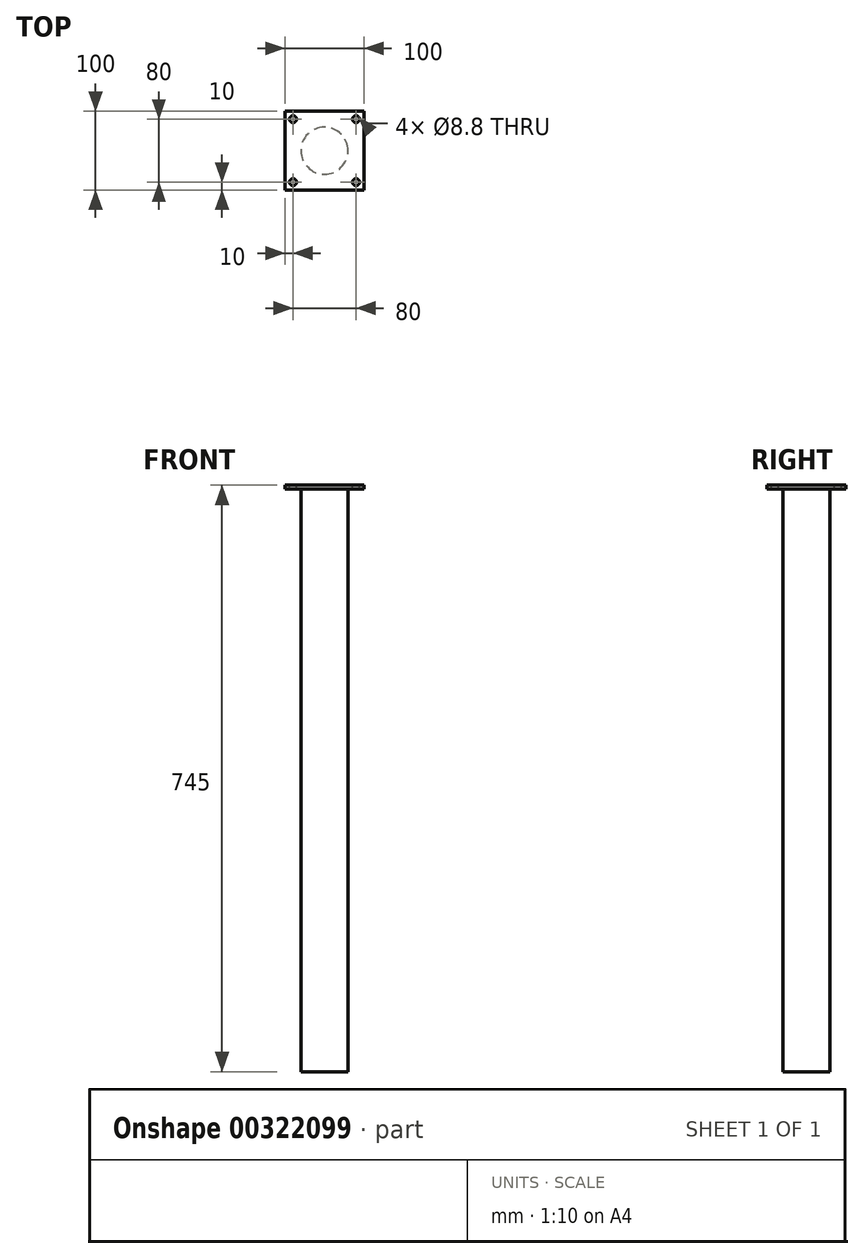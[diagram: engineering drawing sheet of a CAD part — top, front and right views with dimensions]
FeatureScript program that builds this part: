
annotation { "Feature Type Name" : "Feature", "Feature Type Description" : "" }
export const myFeature = defineFeature(function(context is Context, id is Id, definition is map)
    precondition{}
    {
        {
            var Q0;
            Q0=qCreatedBy(makeId("Top.planeOp"),FACE);
            var sketch = newSketch(context, id + "F0", { "sketchPlane" : qUnion([Q0])});
            skCircle(sketch, "E0", {"center": v(0, 0) * mm, "radius": 30 * mm});
            skSolve(sketch);
        }
        {
            var Q0;
            Q0=makeQuery(id+"F0.imprint","IMPRINT",FACE,{"disambiguationData":[TD([[makeQuery(id+"F0.imprint","IMPRINT",EDGE,{"derivedFrom":sQuery(id+"F0.wireOp",EDGE,"E0")}),1.0]])]});
            extrude(context, id + "F1", {"entities" : qUnion([Q0]), "depth" : 740 * mm});
        }
        {
            var Q0;
            Q0=makeQuery(id+"F1.opExtrude","CAP_FACE",FACE,{"disambiguationData":[OSD([sQuery(id+"F0.wireOp",EDGE,"E0")])],"isStart":false});
            var sketch = newSketch(context, id + "F2", { "sketchPlane" : qUnion([Q0])});
            skLineSegment(sketch, "E1.bottom", {"start": v(50, -50) * mm, "end": v(-50, -50) * mm});
            skLineSegment(sketch, "E1.top", {"start": v(50, 50) * mm, "end": v(-50, 50) * mm});
            skLineSegment(sketch, "E1.left", {"start": v(50, -50) * mm, "end": v(50, 50) * mm});
            skLineSegment(sketch, "E1.right", {"start": v(-50, -50) * mm, "end": v(-50, 50) * mm});
            skPoint(sketch, "E1.middle", {"position": v(0, 0) * mm});
            skSolve(sketch);
        }
        {
            var Q0;
            Q0=makeQuery(id+"F2.imprint","IMPRINT",FACE,{"disambiguationData":[TD([[makeQuery(id+"F2.imprint","IMPRINT",EDGE,{"derivedFrom":sQuery(id+"F2.wireOp",EDGE,"E1.bottom")}),-1.0]])]});
            var Q1;
            Q1=makeQuery(id+"F2.imprint","IMPRINT",FACE,{"disambiguationData":[TD([[makeQuery(id+"F2.imprint","IMPRINT",EDGE,{"derivedFrom":makeQuery(id+"F1.opExtrude","CAP_EDGE",EDGE,{"disambiguationData":[OSD([sQuery(id+"F0.wireOp",EDGE,"E0")])],"isStart":false})}),1.0]])]});
            extrude(context, id + "F3", {"entities" : qUnion([Q0, Q1]), "operationType" : NewBodyOperationType.ADD, "depth" : 5 * mm});
        }
        {
            var Q0;
            Q0=makeQuery(id+"F3.opExtrude","CAP_FACE",FACE,{"disambiguationData":[OSD([sQuery(id+"F0.wireOp",EDGE,"E0"),sQuery(id+"F2.wireOp",EDGE,"E1.bottom"),sQuery(id+"F2.wireOp",EDGE,"E1.top"),sQuery(id+"F2.wireOp",EDGE,"E1.left"),sQuery(id+"F2.wireOp",EDGE,"E1.right")])],"isStart":false});
            var sketch = newSketch(context, id + "F4", { "sketchPlane" : qUnion([Q0])});
            skPoint(sketch, "E2", {"position": v(-40, 40) * mm});
            skLineSegment(sketch, "E3", {"start": v(0, 50) * mm, "end": v(0, -50) * mm, "construction": true});
            skLineSegment(sketch, "E4", {"start": v(-50, 0) * mm, "end": v(50, 0) * mm, "construction": true});
            skPoint(sketch, "E5.0.1.0", {"position": v(-40, -40) * mm});
            skPoint(sketch, "E5.1.0.0", {"position": v(40, 40) * mm});
            skPoint(sketch, "E5.1.1.0", {"position": v(40, -40) * mm});
            skPoint(sketch, "E5.2.0.0", {"position": v(120, 40) * mm});
            skPoint(sketch, "E5.2.1.0", {"position": v(120, -40) * mm});
            skLineSegment(sketch, "E5.direction1", {"start": v(-40, 40) * mm, "end": v(40, 40) * mm, "construction": true});
            skLineSegment(sketch, "E5.direction2", {"start": v(-40, 40) * mm, "end": v(-40, -40) * mm, "construction": true});
            skSolve(sketch);
        }
        {
            var Q0;
            Q0=sQuery(id+"F4.wireOp",VERTEX,"E2");
            var Q1;
            Q1=sQuery(id+"F4.wireOp",VERTEX,"E5.1.0.0");
            var Q2;
            Q2=sQuery(id+"F4.wireOp",VERTEX,"E5.1.1.0");
            var Q3;
            Q3=sQuery(id+"F4.wireOp",VERTEX,"E5.0.1.0");
            var Q4;
            Q4=makeQuery(id+"F3.opExtrude","SWEPT_BODY",BODY,{"disambiguationData":[OSD([sQuery(id+"F0.wireOp",EDGE,"E0"),sQuery(id+"F2.wireOp",EDGE,"E1.bottom"),sQuery(id+"F2.wireOp",EDGE,"E1.top"),sQuery(id+"F2.wireOp",EDGE,"E1.left"),sQuery(id+"F2.wireOp",EDGE,"E1.right")])]});
            var Q5;
            Q5=makeQuery(id+"F1.opExtrude","SWEPT_BODY",BODY,{"disambiguationData":[OSD([sQuery(id+"F0.wireOp",EDGE,"E0")])]});
            hole(context, id + "F5", {"style" : HoleStyle.SIMPLE, "endStyle" : HoleEndStyle.THROUGH, "standardTappedOrClearance" : lookupTablePath({ "standard" : "ISO", "fit" : "Normal", "size" : "M8", "type" : "Clearance" }), "standardBlindInLast" : lookupTablePath({ "fit" : "Standard", "standard" : "ISO", "size" : "M8", "type" : "Clearance" }), "holeDiameter" : 8.8 * mm, "tappedDepth" : 12 * mm, "tapClearance" : 3, "locations" : qUnion([Q0, Q1, Q2, Q3]), "scope" : qUnion([Q4, Q5])});
        }
    });
